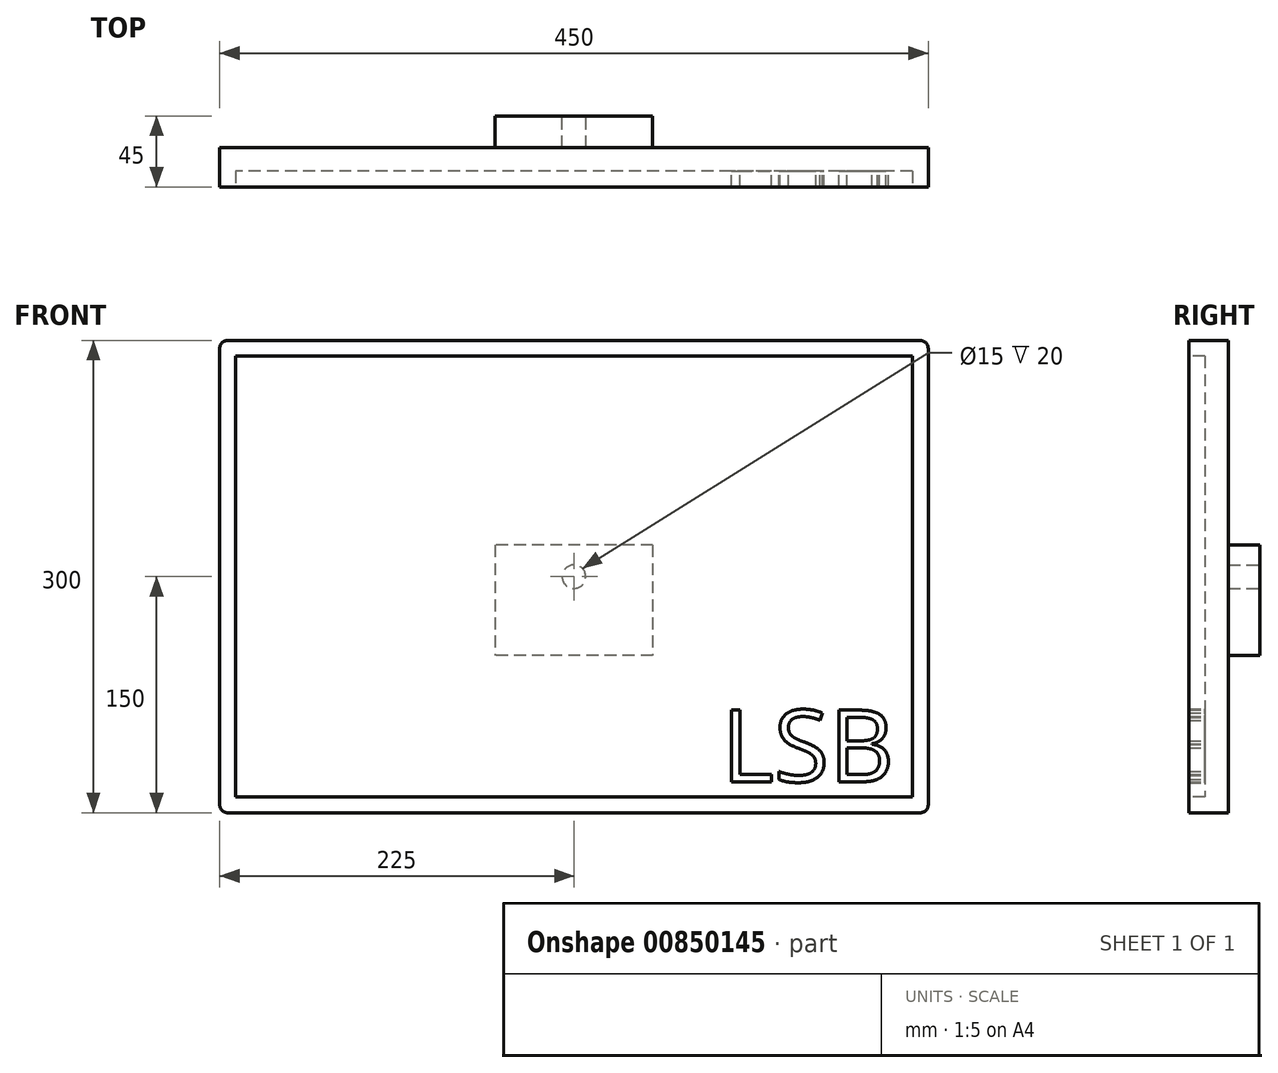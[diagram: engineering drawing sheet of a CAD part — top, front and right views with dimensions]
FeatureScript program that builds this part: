
annotation { "Feature Type Name" : "Feature", "Feature Type Description" : "" }
export const myFeature = defineFeature(function(context is Context, id is Id, definition is map)
    precondition{}
    {
        {
            var Q0;
            Q0=qCreatedBy(makeId("Front.planeOp"),FACE);
            var sketch = newSketch(context, id + "F0", { "sketchPlane" : qUnion([Q0])});
            skLineSegment(sketch, "E0.bottom", {"start": v(-225, 150) * mm, "end": v(225, 150) * mm});
            skLineSegment(sketch, "E0.top", {"start": v(-225, -150) * mm, "end": v(225, -150) * mm});
            skLineSegment(sketch, "E0.left", {"start": v(-225, 150) * mm, "end": v(-225, -150) * mm});
            skLineSegment(sketch, "E0.right", {"start": v(225, 150) * mm, "end": v(225, -150) * mm});
            skSolve(sketch);
        }
        {
            var Q0;
            Q0=makeQuery(id+"F0.imprint","IMPRINT",FACE,{"disambiguationData":[TD([[makeQuery(id+"F0.imprint","IMPRINT",EDGE,{"derivedFrom":sQuery(id+"F0.wireOp",EDGE,"E0.bottom")}),-1.0]])]});
            extrude(context, id + "F1", {"entities" : qUnion([Q0]), "depth" : 25 * mm, "offsetDistance" : 25 * mm});
        }
        {
            var Q0;
            Q0=makeQuery(id+"F1.opExtrude","CAP_FACE",FACE,{"disambiguationData":[OSD([sQuery(id+"F0.wireOp",EDGE,"E0.bottom"),sQuery(id+"F0.wireOp",EDGE,"E0.top"),sQuery(id+"F0.wireOp",EDGE,"E0.left"),sQuery(id+"F0.wireOp",EDGE,"E0.right")])],"isStart":false});
            var sketch = newSketch(context, id + "F2", { "sketchPlane" : qUnion([Q0])});
            skLineSegment(sketch, "E1.0", {"start": v(-215, 140) * mm, "end": v(-215, -140) * mm});
            skLineSegment(sketch, "E1.1", {"start": v(215, 140) * mm, "end": v(-215, 140) * mm});
            skLineSegment(sketch, "E1.2", {"start": v(215, -140) * mm, "end": v(215, 140) * mm});
            skLineSegment(sketch, "E1.3", {"start": v(-215, -140) * mm, "end": v(215, -140) * mm});
            skSolve(sketch);
        }
        {
            var Q0;
            Q0=makeQuery(id+"F2.imprint","IMPRINT",FACE,{"disambiguationData":[TD([[makeQuery(id+"F2.imprint","IMPRINT",EDGE,{"derivedFrom":sQuery(id+"F2.wireOp",EDGE,"E1.0")}),1.0]])]});
            extrude(context, id + "F3", {"entities" : qUnion([Q0]), "operationType" : NewBodyOperationType.REMOVE, "oppositeDirection" : true, "depth" : 10 * mm, "offsetDistance" : 25 * mm});
        }
        {
            var Q0;
            Q0=makeQuery(id+"F1.opExtrude","CAP_FACE",FACE,{"disambiguationData":[OSD([sQuery(id+"F0.wireOp",EDGE,"E0.bottom"),sQuery(id+"F0.wireOp",EDGE,"E0.top"),sQuery(id+"F0.wireOp",EDGE,"E0.left"),sQuery(id+"F0.wireOp",EDGE,"E0.right")])],"isStart":true});
            var sketch = newSketch(context, id + "F4", { "sketchPlane" : qUnion([Q0])});
            skLineSegment(sketch, "E2.bottom", {"start": v(-50, 20) * mm, "end": v(50, 20) * mm});
            skLineSegment(sketch, "E2.top", {"start": v(-50, -50) * mm, "end": v(50, -50) * mm});
            skLineSegment(sketch, "E2.left", {"start": v(-50, 20) * mm, "end": v(-50, -50) * mm});
            skLineSegment(sketch, "E2.right", {"start": v(50, 20) * mm, "end": v(50, -50) * mm});
            skSolve(sketch);
        }
        {
            var Q0;
            Q0=makeQuery(id+"F4.imprint","IMPRINT",FACE,{"disambiguationData":[TD([[makeQuery(id+"F4.imprint","IMPRINT",EDGE,{"derivedFrom":sQuery(id+"F4.wireOp",EDGE,"E2.bottom")}),-1.0]])]});
            extrude(context, id + "F5", {"entities" : qUnion([Q0]), "operationType" : NewBodyOperationType.ADD, "depth" : 20 * mm, "offsetDistance" : 25 * mm});
        }
        {
            var Q0;
            Q0=makeQuery(id+"F5.opExtrude","CAP_FACE",FACE,{"disambiguationData":[OSD([sQuery(id+"F4.wireOp",EDGE,"E2.bottom"),sQuery(id+"F4.wireOp",EDGE,"E2.top"),sQuery(id+"F4.wireOp",EDGE,"E2.left"),sQuery(id+"F4.wireOp",EDGE,"E2.right")])],"isStart":false});
            var sketch = newSketch(context, id + "F6", { "sketchPlane" : qUnion([Q0])});
            skCircle(sketch, "E3", {"center": v(0, 0) * mm, "radius": 7.5 * mm});
            skSolve(sketch);
        }
        {
            var Q0;
            Q0=makeQuery(id+"F6.imprint","IMPRINT",FACE,{"disambiguationData":[TD([[makeQuery(id+"F6.imprint","IMPRINT",EDGE,{"derivedFrom":sQuery(id+"F6.wireOp",EDGE,"E3")}),1.0]])]});
            extrude(context, id + "F7", {"entities" : qUnion([Q0]), "operationType" : NewBodyOperationType.REMOVE, "oppositeDirection" : true, "depth" : 20 * mm, "offsetDistance" : 25 * mm});
        }
        {
            var Q0;
            Q0=makeQuery(id+"F3.boolean.opBoolean","COPY",FACE,{"derivedFrom":makeQuery(id+"F3.opExtrude","CAP_FACE",FACE,{"disambiguationData":[OSD([sQuery(id+"F2.wireOp",EDGE,"E1.0"),sQuery(id+"F2.wireOp",EDGE,"E1.1"),sQuery(id+"F2.wireOp",EDGE,"E1.2"),sQuery(id+"F2.wireOp",EDGE,"E1.3")])],"isStart":false})});
            var sketch = newSketch(context, id + "F8", { "sketchPlane" : qUnion([Q0])});
            skText(sketch, "E4", { "text": "LSB", "fontName": "OpenSans-Regular.ttf"});
            const initialGuessF8  = {"E4": [0.0939, -0.13028, 1, 0, 0.04588]};
            skSetInitialGuess(sketch, initialGuessF8);
            skSolve(sketch);
        }
        {
            var Q0;
            Q0 = qSketchRegion(id + "F8", true);
            extrude(context, id + "F9", {"entities" : qUnion([Q0]), "operationType" : NewBodyOperationType.ADD, "depth" : 10 * mm, "offsetDistance" : 25 * mm});
        }
        {
            var Q0;
            Q0=makeQuery(id+"F1.opExtrude","SWEPT_EDGE",EDGE,{"disambiguationData":[OSD([sQuery(id+"F0.wireOp",EDGE,"E0.bottom"),sQuery(id+"F0.wireOp",EDGE,"E0.left")])]});
            var Q1;
            Q1=makeQuery(id+"F1.opExtrude","SWEPT_EDGE",EDGE,{"disambiguationData":[OSD([sQuery(id+"F0.wireOp",EDGE,"E0.bottom"),sQuery(id+"F0.wireOp",EDGE,"E0.right")])]});
            var Q2;
            Q2=makeQuery(id+"F1.opExtrude","SWEPT_EDGE",EDGE,{"disambiguationData":[OSD([sQuery(id+"F0.wireOp",EDGE,"E0.top"),sQuery(id+"F0.wireOp",EDGE,"E0.right")])]});
            var Q3;
            Q3=makeQuery(id+"F1.opExtrude","SWEPT_EDGE",EDGE,{"disambiguationData":[OSD([sQuery(id+"F0.wireOp",EDGE,"E0.top"),sQuery(id+"F0.wireOp",EDGE,"E0.left")])]});
            fillet(context, id + "F10", {"entities" : qUnion([Q0, Q1, Q2, Q3]), "radius" : 5 * mm, "tangentPropagation" : true, "allowEdgeOverflow" : false});
        }
    });
